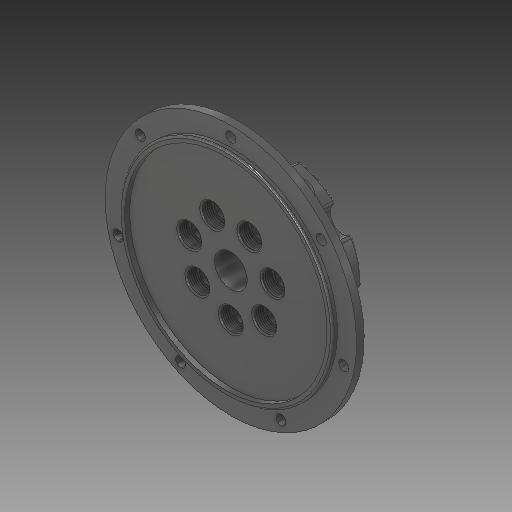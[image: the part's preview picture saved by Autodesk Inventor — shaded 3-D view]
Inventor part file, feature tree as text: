
AUTODESK INVENTOR PART (.ipt)
format: ipt  version: 2018 (Build 220112000, 112)  size: 850,432 bytes
history: native  units: mm
features: sketch x10, extrude x7, thread x7, fillet x2, plane x2, revolve x1, sweep x1, other x1, pattern_circular x1, chamfer x1
ambient origin geometry x8: Origin, YZ Plane, XZ Plane, XY Plane, X Axis, Y Axis, Z Axis, Center Point
bodies: Solid1 (feature_tree)
feature tree (33):
  revolve  "Revolution1"  [1 undecoded]
  extrude  "Extrusion1"  Depth=40.25mm
  fillet  "Fillet1"  Radius=50.0mm
  extrude  "Extrusion2"  Depth=5.0mm
  plane  "Work Plane1"
  extrude  "Extrusion3"  Depth=0.75mm
  extrude  "Extrusion4"  TaperAngle=90.0deg  [1 undecoded]
  sweep  "Sweep1"
  fillet  "Fillet2"  Radius=10.0mm
  plane  "Work Plane2"
  extrude  "Extrusion5"  Depth=1.0mm
  extrude  "Extrusion6"  Depth=9.5mm
  other  "Work Axis1"
  pattern_circular  "Circular Pattern1"  [2 undecoded]
  extrude  "Extrusion7"  Depth=10.0mm TaperAngle=0.0deg
  thread  "Thread1"  [1 undecoded]
  thread  "Thread2"  [1 undecoded]
  thread  "Thread3"  [1 undecoded]
  thread  "Thread4"  [1 undecoded]
  thread  "Thread5"  [1 undecoded]
  thread  "Thread6"  [1 undecoded]
  thread  "Thread7"  [1 undecoded]
  chamfer  "Chamfer1"  Distance=3.0mm
  sketch  "Sketch1"  dims[d0=6.5mm d1=22.0mm]
  sketch  "Sketch2"  dims[d2=40.25mm d3=42.375mm d4=50.0mm]
  sketch  "Sketch3"  dims[d5=3.0mm d6=5.0mm]
  sketch  "Sketch4"  dims[d8=30.0mm d11=0.75mm]
  sketch  "Sketch5"  dims[d12=1.4mm d13=90.0deg]
  sketch  "Sketch6"  dims[d14=10.0mm d15=70.0mm d17=360.0deg d19=10.0mm d20=0.0mm]
  sketch  "Sketch7"  dims[d21=1.0mm d22=2.5mm]
  sketch  "Sketch8"  dims[d23=9.5mm d24=9.5mm]
  sketch  "Sketch9"  dims[d25=50.5mm d26=0.0mm]
  sketch  "Sketch10"  dims[d27=25.0mm d28=5.0mm d29=2.8mm d30=1.4mm d31=0.0mm d32=0.0mm d33=9.0mm d34=17.0mm d35=7.0mm d36=4.2mm d37=0.0mm d38=1.7mm d39=3.5mm d40=3.5mm d41=3.0mm d42=0.0mm d43=0.0mm d44=2.0mm d45=-30.0mm d46=12.15mm d47=2.0mm d48=0.0mm d49=10.42mm d50=5.0mm d51=0.0mm d52=70.0mm d53=360.0deg d55=4.0mm d56=46.0mm d57=70.0mm d59=360.0deg d61=5.0mm d62=0.0mm d63=10.0mm d64=0.0mm d65=10.0mm d66=0.0mm d67=10.0mm d68=0.0mm d69=10.0mm d70=0.0mm d71=10.0mm d72=0.0mm d73=10.0mm d74=0.0mm d75=10.0mm d76=0.0mm d77=0.5mm d78=2.0mm d79=45.0deg d81=9.5mm]
note: 11 required parameter values undecoded (feature->parameter linkage not recoverable at this tier; creation-order binding heuristic only, values carry confidence <= 0.55)